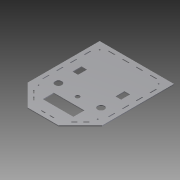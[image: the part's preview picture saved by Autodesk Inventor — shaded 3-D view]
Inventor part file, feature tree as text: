
AUTODESK INVENTOR PART (.ipt)
format: ipt  version: 2012 (Build 160160000, 160)  size: 266,752 bytes
history: native  units: mm
features: sketch x2, extrude x1, hole x1
ambient origin geometry x8: Origin, YZ Plane, XZ Plane, XY Plane, X Axis, Y Axis, Z Axis, Center Point
bodies: Solid1 (feature_tree)
feature tree (4):
  extrude  "Extrusion1"  Depth=2.0mm TaperAngle=0.0deg
  hole  "Hole1"  [1 undecoded]
  sketch  "Sketch1"  dims[d44=10.0mm d45=2.0mm d46=10.0mm d47=2.0mm d48=10.0mm d49=2.0mm d50=10.0mm d51=2.0mm d52=10.0mm d53=10.0mm d54=2.0mm d55=10.0mm d56=2.0mm d57=10.0mm d58=15.0mm d59=2.0mm d60=15.0mm d61=18.0mm d62=15.0mm d63=17.0mm d64=2.0mm d65=15.0mm d66=15.0mm d67=18.0mm d68=15.0mm d69=17.0mm d70=15.0mm d71=18.0mm d72=15.0mm d73=18.0mm d74=219.764931mm d75=174.51mm d76=3.0mm d77=3.0mm d78=71.8mm d79=25.8mm d80=35.0mm d81=16.0mm d82=25.0mm d83=13.0mm d84=21.0mm d85=40.0mm d86=9.7mm d87=20.0mm d88=2.0mm d89=0.0mm]
  sketch  "Sketch2"  dims[d90=10.0mm d91=2.0mm d92=10.0mm d93=2.0mm d94=10.0mm d95=2.0mm d96=10.0mm d97=2.0mm d98=10.0mm d99=10.0mm d100=2.0mm d101=10.0mm d102=2.0mm d103=10.0mm d104=15.0mm d105=2.0mm d106=15.0mm d107=18.0mm d108=15.0mm d109=17.0mm d110=2.0mm d111=15.0mm d112=15.0mm d113=18.0mm d114=15.0mm d115=17.0mm d116=15.0mm d117=18.0mm d118=15.0mm d119=18.0mm d120=219.764931mm d121=174.51mm d122=3.0mm d123=3.0mm d124=71.8mm d125=25.8mm d126=35.0mm d127=16.0mm d128=25.0mm d129=13.0mm d130=21.0mm d131=40.0mm d132=9.7mm d133=20.0mm d134=3.0mm d135=6.0mm d136=4.0mm d137=2.0mm d138=90.0deg d139=8.0mm d140=20.594885mm]
note: 1 required parameter value undecoded (feature->parameter linkage not recoverable at this tier; creation-order binding heuristic only, values carry confidence <= 0.55)
